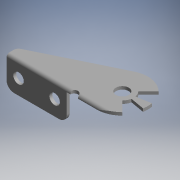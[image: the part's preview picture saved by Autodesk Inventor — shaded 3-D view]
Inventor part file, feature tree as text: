
AUTODESK INVENTOR PART (.ipt)
format: ipt  version: 2017.3 (Build 213256000, 256)  size: 163,840 bytes
history: native  units: mm (DEFAULTED — no unit token found)
features: other x21, sketch x6, extrude x4, hole x2
ambient origin geometry x8: Origin, YZ Plane, XZ Plane, XY Plane, X Axis, Y Axis, Z Axis, Center Point
bodies: Solid1 (feature_tree)
feature tree (33):
  extrude  "Extrusion1"  Depth=120.0mm TaperAngle=0.0deg
  extrude  "Extrusion2"  Depth=2.0mm TaperAngle=0.0deg
  extrude  "Extrusion3"  [1 undecoded]
  hole  "Hole1"  [1 undecoded]
  hole  "Hole2"  [1 undecoded]
  extrude  "Extrusion4"  [1 undecoded]
  other  "fix_end_r_XY"
  other  "fix_end_r_YZ"
  other  "fix_end_r_ZX"
  other  "fix_end_r_X"
  other  "fix_end_r_Y"
  other  "fix_end_r_Z"
  other  "fix_end_r_Center"
  other  "free_end_r_XY"
  other  "free_end_r_YZ"
  other  "free_end_r_ZX"
  other  "free_end_r_X"
  other  "free_end_r_Y"
  other  "free_end_r_Z"
  other  "free_end_r_Center"
  other  "r_XY"
  other  "r_YZ"
  other  "r_ZX"
  other  "r_X"
  other  "r_Y"
  other  "r_Z"
  other  "r_Center"
  sketch  "Sketch_1"  dims[d0=20.0mm d1=0.0mm d2=120.0mm d3=0.0mm]
  sketch  "Sketch_2"  dims[d4=34.0mm d5=0.0mm]
  sketch  "Sketch_3"  dims[d6=7.0mm d7=6.0mm d8=4.0mm d9=2.0mm d10=90.0deg d11=2.0mm d12=0.0mm]
  sketch  "Sketch4"  dims[d13=7.0mm d14=6.0mm d15=4.0mm d16=2.0mm d17=90.0deg d18=2.0mm d19=0.0mm d20=20.0mm d21=0.0mm]
  sketch  "Sketch5"  dims[d22=0.0mm d23=0.0mm]
  sketch  "Sketch_7"
note: 4 required parameter values undecoded (feature->parameter linkage not recoverable at this tier; creation-order binding heuristic only, values carry confidence <= 0.55)
